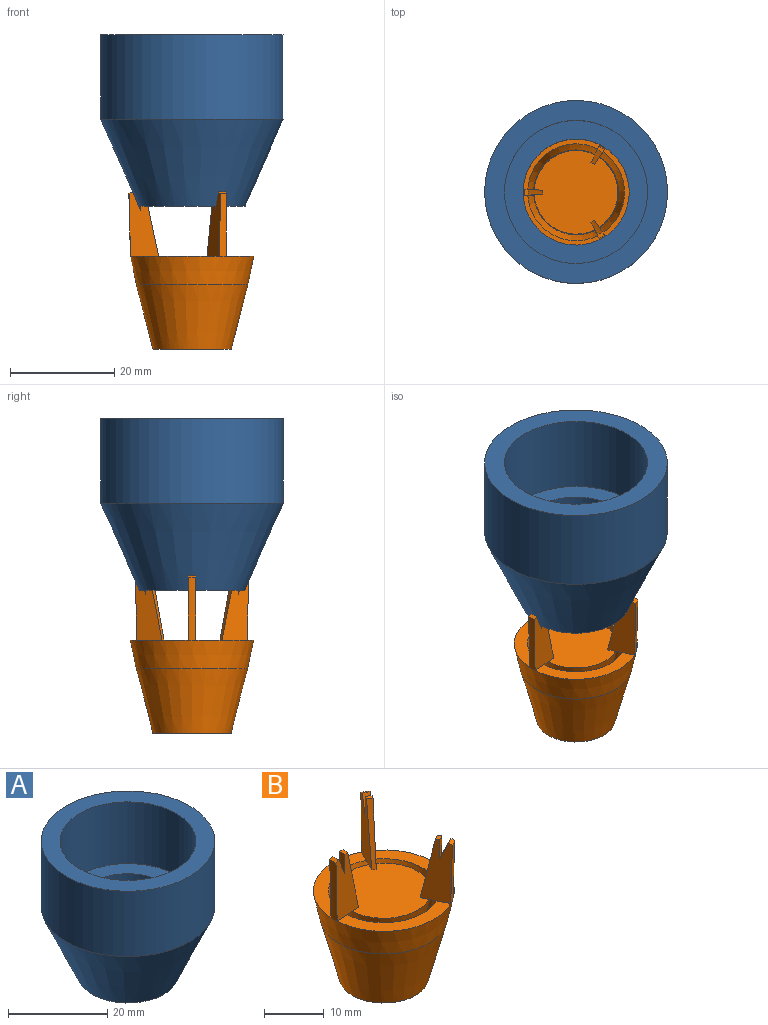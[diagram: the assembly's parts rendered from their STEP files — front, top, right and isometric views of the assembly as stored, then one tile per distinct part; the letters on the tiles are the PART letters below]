
ASSEMBLY  parts=2 mates=1
PART A: 6 faces, bbox 35.1x35.1x32.8 mm
  f0: cone r=17.53mm half-angle=23.8deg, axis (0,0,1), area 1585.3mm2, adj f1,f5
  f1: cylinder r=10.16mm len=20.32mm, axis (0,0,-1), area 1122mm2, adj f0,f2
  f2: plane 27.43x27.43mm, normal (0,0,1), area 266.7mm2, adj f1,f3
  f3: cylinder r=13.72mm len=27.43mm, axis (0,0,-1), area 1313.4mm2, adj f2,f4
  f4: plane 35.05x35.05mm, normal (0,0,1), area 374mm2, adj f3,f5
  f5: cylinder r=17.53mm len=35.05mm, axis (0,0,-1), area 1777.8mm2, adj f0,f4
PART B: 64 faces, bbox 24.3x24x30.8 mm
  f0: plane 17.08x11.26mm, normal (0,0,1), area 52.9mm2, adj f22,f23,f45,f62
  f1: plane 19.72x6.7mm, normal (0,0,1), area 52.9mm2, adj f22,f23,f53,f63
  f2: plane 17.08x11.26mm, normal (0,0,1), area 52.9mm2, adj f22,f23,f44,f54
  f3: plane 3.71x3.48mm, normal (0,-1,0), area 7.3mm2, adj f8,f18,f25,f34
  f4: plane 3.71x3.48mm, normal (0,1,0), area 7.3mm2, adj f10,f12,f25,f31
  f5: plane 3.71x3.48mm, normal (0,1,0), area 7.3mm2, adj f7,f14,f25,f36
  f6: plane 3.71x3.48mm, normal (0,-1,0), area 7.3mm2, adj f9,f17,f25,f29
  f7: plane 3.71x3.48mm, normal (1,0,0), area 7.3mm2, adj f5,f15,f25,f32
  f8: plane 3.71x3.48mm, normal (-1,0,0), area 7.3mm2, adj f3,f19,f25,f30
  f9: plane 3.71x3.48mm, normal (1,0,0), area 7.3mm2, adj f6,f16,f25,f33
  f10: plane 3.71x3.49mm, normal (-1,0,0), area 7.3mm2, adj f4,f13,f25,f35
  f11: plane 14.97x14.97mm, normal (0,0,-1), area 104.2mm2, adj f12,f13,f14,f15,f16,f17,f18,f19
  f12: cylinder r=0.51mm len=5.03mm, axis (1,0,0), area 4mm2, adj f4,f11,f13,f20,f31
  f13: cylinder r=0.51mm len=5.03mm, axis (0,1,0), area 4mm2, adj f10,f11,f12,f20,f35
  f14: cylinder r=0.51mm len=5.03mm, axis (1,0,0), area 4mm2, adj f5,f11,f15,f20,f36
  f15: cylinder r=0.51mm len=5.03mm, axis (0,-1,0), area 4mm2, adj f7,f11,f14,f20,f32
  f16: cylinder r=0.51mm len=5.03mm, axis (0,-1,0), area 4mm2, adj f9,f11,f17,f20,f33
  f17: cylinder r=0.51mm len=5.03mm, axis (-1,0,0), area 4mm2, adj f6,f11,f16,f20,f29
  f18: cylinder r=0.51mm len=5.03mm, axis (-1,0,0), area 4mm2, adj f3,f11,f19,f20,f34
  f19: cylinder r=0.51mm len=5.03mm, axis (0,1,0), area 4mm2, adj f8,f11,f18,f20,f30
  f20: cone r=8.08mm half-angle=14.5deg, axis (0,0,1), area 500.8mm2, adj f11,f12,f13,f14,f15,f16,f17,f18
  f21: revolved ~16.35x16.35mm, area 40.9mm2, adj f20,f22
  f22: cone r=9.29mm half-angle=11.9deg, axis (0,0,1), area 294.9mm2, adj f0,f1,f2,f21,f37,f46,f55
  f23: cone r=10.67mm half-angle=11.9deg, axis (0,0,1), area 394.1mm2, adj f0,f1,f2,f24,f42,f51,f60
  f24: cone r=7.49mm half-angle=14.5deg, axis (0,0,1), area 726.3mm2, adj f11,f23
  f25: cone r=6.27mm half-angle=29.7deg, axis (0,0,1), area 212.4mm2, adj f3,f4,f5,f6,f7,f8,f9,f10
  f26: plane 16.03x16.02mm, normal (0,0,1), area 197.6mm2, adj f27,f43,f44,f45,f52,f53,f54,f61
  f27: cone r=8.02mm half-angle=11.9deg, axis (0,0,1), area 239.1mm2, adj f26,f28,f37,f46,f55
  f28: torus R=0.75mm, axis (0,0,-1), area 82.7mm2, adj f25,f27
  f29: plane 7.95x4.2mm, normal (0.15,-0.99,0.07), area 16.6mm2, adj f6,f17,f20,f25,f36
  f30: plane 7.95x4.2mm, normal (-0.99,-0.15,0.07), area 16.6mm2, adj f8,f19,f20,f25,f33
  f31: plane 7.95x4.2mm, normal (-0.15,0.99,0.07), area 16.6mm2, adj f4,f12,f20,f25,f34
  f32: plane 7.95x4.2mm, normal (0.99,0.15,0.07), area 16.6mm2, adj f7,f15,f20,f25,f35
  f33: plane 7.95x4.2mm, normal (0.99,-0.15,0.07), area 16.6mm2, adj f9,f16,f20,f25,f30
  f34: plane 7.95x4.2mm, normal (-0.15,-0.99,0.07), area 16.6mm2, adj f3,f18,f20,f25,f31
  f35: plane 7.95x4.2mm, normal (-0.99,0.15,0.07), area 16.6mm2, adj f10,f13,f20,f25,f32
  f36: plane 7.95x4.2mm, normal (0.15,0.99,0.07), area 16.6mm2, adj f5,f14,f20,f25,f29
  f37: plane 1.29x1.13mm, normal (0,0,-1), area 1.3mm2, adj f22,f27,f44,f45
  f38: plane 1.21x0.76mm, normal (0,0,1), area 0.9mm2, adj f39,f43,f44,f45
  f39: cylinder r=9.88mm len=3.86mm, axis (0,0,-1), area 4.7mm2, adj f38,f40,f44,f45
  f40: cone r=9.88mm half-angle=23.8deg, axis (0,0,1), area 5mm2, adj f39,f41,f44,f45
  f41: cone r=12.12mm half-angle=66.2deg, axis (0,0,-1), area 1.1mm2, adj f40,f42,f44,f45
  f42: cone r=12.12mm half-angle=1.4deg, axis (0,0,1), area 17.7mm2, adj f23,f41,f44,f45
  f43: cone r=9.14mm half-angle=12.2deg, axis (0,0,1), area 12.3mm2, adj f26,f38,f44,f45
  f44: plane 12.7x5.7mm, normal (0.06,-1,0), area 49.8mm2, adj f2,f26,f37,f38,f39,f40,f41,f42
  f45: plane 12.7x5.7mm, normal (0.06,1,0), area 49.8mm2, adj f0,f26,f37,f38,f39,f40,f41,f42
  f46: plane 1.63x1.55mm, normal (0,0,-1), area 1.3mm2, adj f22,f27,f53,f54
  f47: plane 1.37x1.22mm, normal (0,0,1), area 0.9mm2, adj f48,f52,f53,f54
  f48: cylinder r=9.88mm len=3.86mm, axis (0,0,-1), area 4.7mm2, adj f47,f49,f53,f54
  f49: cone r=9.88mm half-angle=23.8deg, axis (0,0,1), area 5mm2, adj f48,f50,f53,f54
  f50: cone r=12.12mm half-angle=66.2deg, axis (0,0,-1), area 1.1mm2, adj f49,f51,f53,f54
  f51: cone r=12.12mm half-angle=1.4deg, axis (0,0,1), area 17.7mm2, adj f23,f50,f53,f54
  f52: cone r=9.14mm half-angle=12.2deg, axis (0,0,1), area 12.3mm2, adj f26,f47,f53,f54
  f53: plane 12.7x4.76mm, normal (0.83,0.55,0), area 49.8mm2, adj f1,f26,f46,f47,f48,f49,f50,f51
  f54: plane 12.7x5.11mm, normal (-0.89,-0.45,0), area 49.8mm2, adj f2,f26,f46,f47,f48,f49,f50,f51
  f55: plane 1.63x1.55mm, normal (0,0,-1), area 1.3mm2, adj f22,f27,f62,f63
  f56: plane 1.37x1.22mm, normal (0,0,1), area 0.9mm2, adj f57,f61,f62,f63
  f57: cylinder r=9.88mm len=3.86mm, axis (0,0,-1), area 4.7mm2, adj f56,f58,f62,f63
  f58: cone r=9.88mm half-angle=23.8deg, axis (0,0,1), area 5mm2, adj f57,f59,f62,f63
  f59: cone r=12.12mm half-angle=66.2deg, axis (0,0,-1), area 1.1mm2, adj f58,f60,f62,f63
  f60: cone r=12.12mm half-angle=1.4deg, axis (0,0,1), area 17.7mm2, adj f23,f59,f62,f63
  f61: cone r=9.14mm half-angle=12.2deg, axis (0,0,1), area 12.3mm2, adj f26,f56,f62,f63
  f62: plane 12.7x5.11mm, normal (-0.89,0.45,0), area 49.8mm2, adj f0,f26,f55,f56,f57,f58,f59,f60
  f63: plane 12.7x4.76mm, normal (0.83,-0.55,0), area 49.8mm2, adj f1,f26,f55,f56,f57,f58,f59,f60
PLACE A at identity fixed
PLACE B t=(0,0,0.51)mm
MATE slider A.f0 <-> B.f22  axis (0,0,1) through (0,0,17.58)mm
